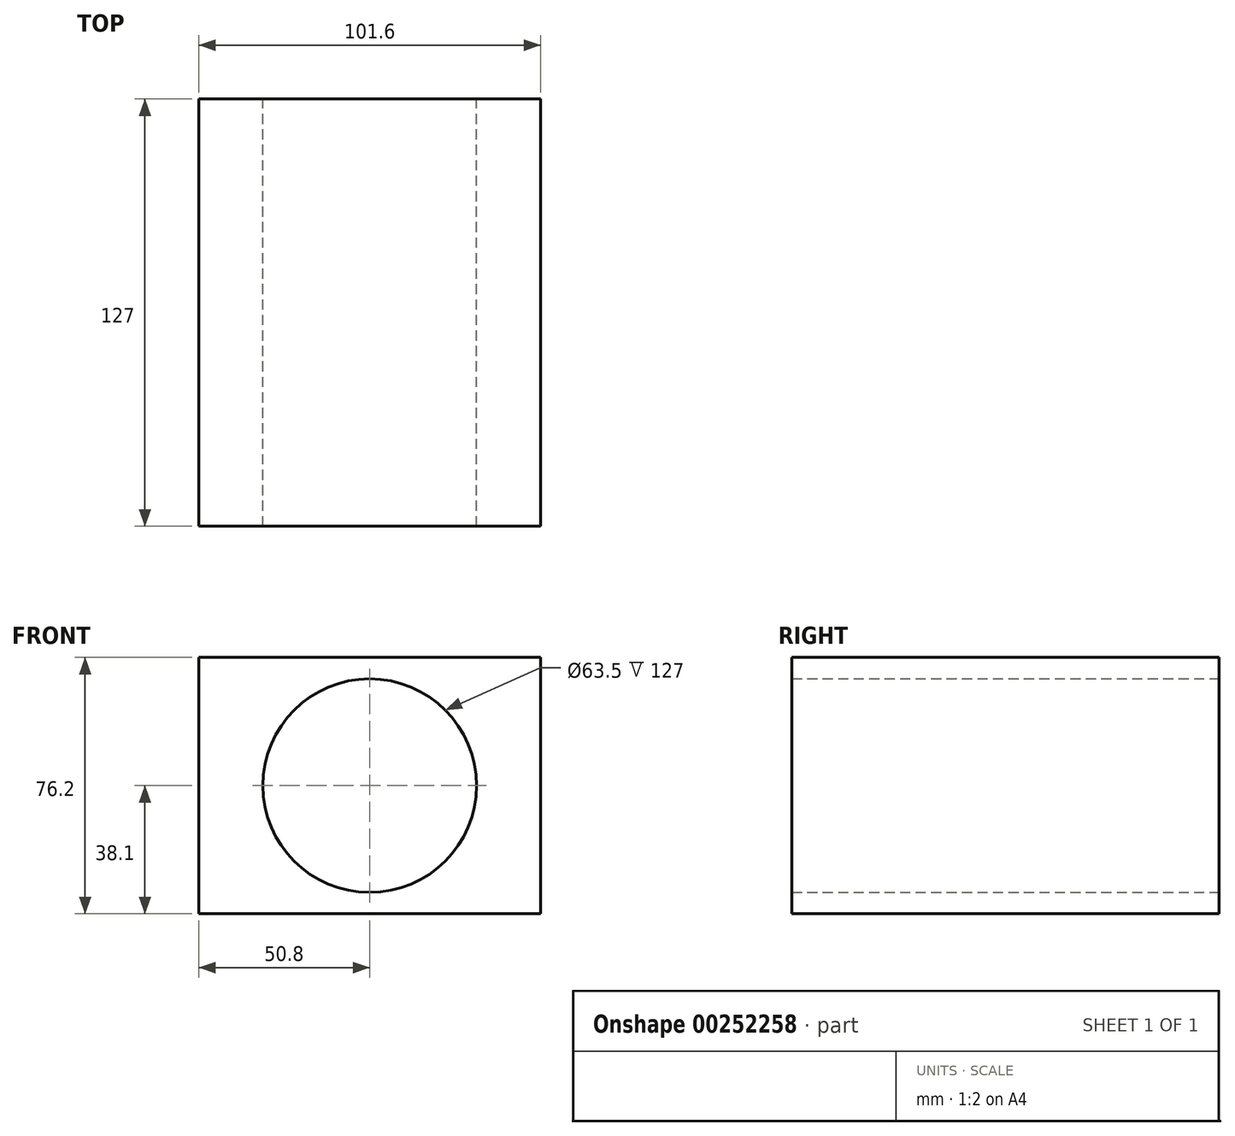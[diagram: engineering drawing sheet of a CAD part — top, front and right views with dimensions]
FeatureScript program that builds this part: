
annotation { "Feature Type Name" : "Feature", "Feature Type Description" : "" }
export const myFeature = defineFeature(function(context is Context, id is Id, definition is map)
    precondition{}
    {
        {
            var Q0;
            Q0=qCreatedBy(makeId("Front.planeOp"),FACE);
            var sketch = newSketch(context, id + "F0", { "sketchPlane" : qUnion([Q0])});
            skLineSegment(sketch, "E0.bottom", {"start": v(-50.8, 38.1) * mm, "end": v(50.8, 38.1) * mm});
            skLineSegment(sketch, "E0.top", {"start": v(-50.8, -38.1) * mm, "end": v(50.8, -38.1) * mm});
            skLineSegment(sketch, "E0.left", {"start": v(-50.8, 38.1) * mm, "end": v(-50.8, -38.1) * mm});
            skLineSegment(sketch, "E0.right", {"start": v(50.8, 38.1) * mm, "end": v(50.8, -38.1) * mm});
            skPoint(sketch, "E0.middle", {"position": v(0, 0) * mm});
            skCircle(sketch, "E1", {"center": v(0, 0) * mm, "radius": 31.75 * mm});
            skSolve(sketch);
        }
        {
            var Q0;
            Q0=makeQuery(id+"F0.imprint","IMPRINT",FACE,{"disambiguationData":[TD([[makeQuery(id+"F0.imprint","IMPRINT",EDGE,{"derivedFrom":sQuery(id+"F0.wireOp",EDGE,"E0.bottom")}),-1.0]])]});
            extrude(context, id + "F1", {"entities" : qUnion([Q0]), "depth" : 127 * mm});
        }
    });
